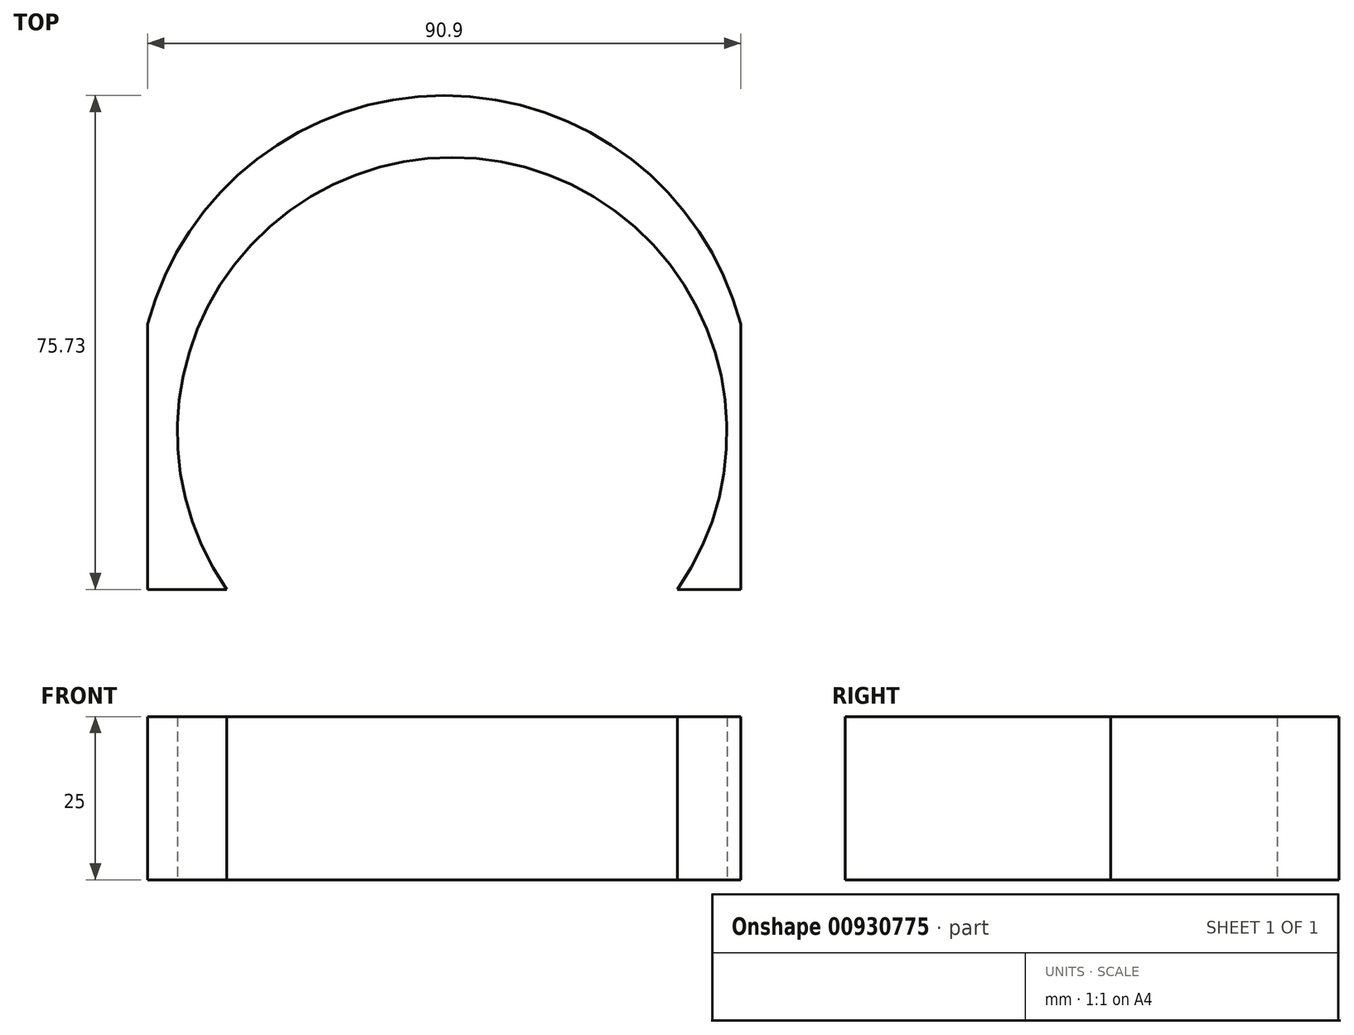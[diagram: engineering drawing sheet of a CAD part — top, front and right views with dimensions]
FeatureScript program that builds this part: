
annotation { "Feature Type Name" : "Feature", "Feature Type Description" : "" }
export const myFeature = defineFeature(function(context is Context, id is Id, definition is map)
    precondition{}
    {
        {
            var Q0;
            Q0=qCreatedBy(makeId("Top.planeOp"),FACE);
            var sketch = newSketch(context, id + "F0", { "sketchPlane" : qUnion([Q0])});
            skLineSegment(sketch, "E0.bottom", {"start": v(45.45, -40.7) * mm, "end": v(35.76, -40.7) * mm});
            skLineSegment(sketch, "E0.left", {"start": v(45.45, -40.7) * mm, "end": v(45.45, 0) * mm});
            skLineSegment(sketch, "E0.right", {"start": v(-45.45, -40.7) * mm, "end": v(-45.45, 0) * mm});
            skPoint(sketch, "E0.middle", {"position": v(0, 0) * mm});
            skPoint(sketch, "E1.visualSharp", {"position": v(-45.45, 40.7) * mm});
            skArc(sketch, "E1.filletArc", {"start": v(-40.45, 40.7) * mm, "mid": v(-43.98, 39.23) * mm, "end": v(-45.45, 35.7) * mm});
            skPoint(sketch, "E2.visualSharp", {"position": v(45.45, 40.7) * mm});
            skArc(sketch, "E2.filletArc", {"start": v(45.45, 35.7) * mm, "mid": v(43.98, 39.23) * mm, "end": v(40.45, 40.7) * mm});
            skArc(sketch, "E3", {"start": v(45.45, 0) * mm, "mid": v(0, 35.03) * mm, "end": v(-45.45, 0) * mm});
            skPoint(sketch, "E3.endSnap0", {"position": v(-45.45, -2.5) * mm});
            skArc(sketch, "E4", {"start": v(35.76, -40.7) * mm, "mid": v(1.23, 25.54) * mm, "end": v(-33.3, -40.7) * mm});
            skLineSegment(sketch, "E5.trimOffspring", {"start": v(-33.3, -40.7) * mm, "end": v(-45.45, -40.7) * mm});
            skSolve(sketch);
        }
        {
            var Q0;
            Q0=makeQuery(id+"F0.imprint","IMPRINT",FACE,{"disambiguationData":[TD([[makeQuery(id+"F0.imprint","IMPRINT",EDGE,{"derivedFrom":sQuery(id+"F0.wireOp",EDGE,"E0.bottom")}),-1.0]])]});
            extrude(context, id + "F1", {"entities" : qUnion([Q0]), "depth" : 25 * mm, "offsetDistance" : 25 * mm});
        }
    });
